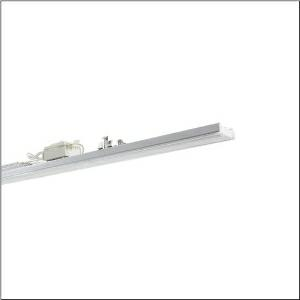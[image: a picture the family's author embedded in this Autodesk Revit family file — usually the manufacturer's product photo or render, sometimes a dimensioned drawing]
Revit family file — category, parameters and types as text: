
# Revit family: licross_21_recessed_mo_52tl11mn4a5g
name_source: partatom
category: Lighting Fixtures
units: mm (PartAtom-declared; Revit-internal decimal feet)

## family parameters
Cut with Voids When Loaded = No
Host = Face
Light Source = No
Part Type = Normal
Room Calculation Point = No
Round Connector Dimension = Use Diameter
Shared = No

## types (1)
- --- (1 x LED, 10830 lm, 60.5 W, 4000K)
    Apparent Load = 61 VA
    CIE Flux Codes = 89 96 99 100 100
    Color Rendering = 80
    Color Temperature = 4000K
    Default Elevation = 1800 mm
    Description = Licross 21 Recessed MO, luminaire insert, of sheet steel, galvanised, coil coated, white, length: 1.500mm, width: 66mm, height: 67mm, LED rated luminous flux: 10.820lm, light colour: 840, SDCM (Standard Deviation of Colour Matching)MacAdam ≤ 3 SDCM (initial), control gear: ON/OFF Multilumen, with plug, 3-pole, with phase selection, mains connection: 220..240V, AC, 50/60Hz, rated input power: 61W, internal wiring halogen-free, primary light control with lens, of plastic, primary optical cover: cover, of PMMA, light emission: direct distribution, primary light characteristic: symmetric, protection rating (complete): IP40, insulation class (complete): insulation class I (protective earthing), certification: CE, ENEC, VDE, UKCA, protection symbol: D if used in an environment without relevant dust loads with corresponding accessories, impact resistance: IK06, permissible ambient temperature for indoor applications: -35..+40°C, corresponds to IFS (International Featured Standards) requirements for safety and quality in the food industry, reducing of maximum allowable ambient temperature of 5°C with ceiling mounting, LABS conformity tested according to VDMA 24364:2018-05, The light source and the operating device comply with the requirements of the Ecodesign Regulation (EU) 2019/2020 and are replaceable in accordance with this regulation, packaging unit: 1 piece
    Height = 58 mm
    Lamp = 1 x LED
    Lamp Light Flux = 10830 lm
    Lamp Power = 60.5 W
    Lamp count = 1
    Length = 1500 mm
    Luminous efficacy = 179 lm/W
    Manufacturer = Siteco
    ModVariant = No
    Model = 52TL11MN4A5G
    Mounting Place = Ceiling
    Mounting Type = Pendant
    Number of Poles = 1
    OnlyDefault = Yes
    Power Factor = 1
    Product Name = Licross 21 Recessed MO
    Product group = luminaire insert | ceiling pendant
    ProductGroupID = 901
    Protection Class = Protection class I
    Protection Degree = IP 40
    RLX_Detail_Level = 1
    RLX_Emergency_Light_Flux = 0 lm
    RLX_Emergency_Type = 0
    RLX_Emergency_Type_DB = No
    RlxData = <blob elided: 22465 chars, md5=38851f0f>
    Socket = socket
    Standby Power = 0 W
    System Light Flux = 10830 lm
    System Power = 61 W
    Type Comments = factory setting: luminous flux: 100 % | (A | C | E) | 140 mA
    Type Image = l_1296930.jpg
    URL = http://relux.com
    VarID = @adj_107979
    Voltage = 0 V
    Weight = 0.00 kg
    Width = 66 mm

## geometry (parser evidence)
native form markers: Blend x4, Sweep x9
no freeform markers — native parametric forms only
